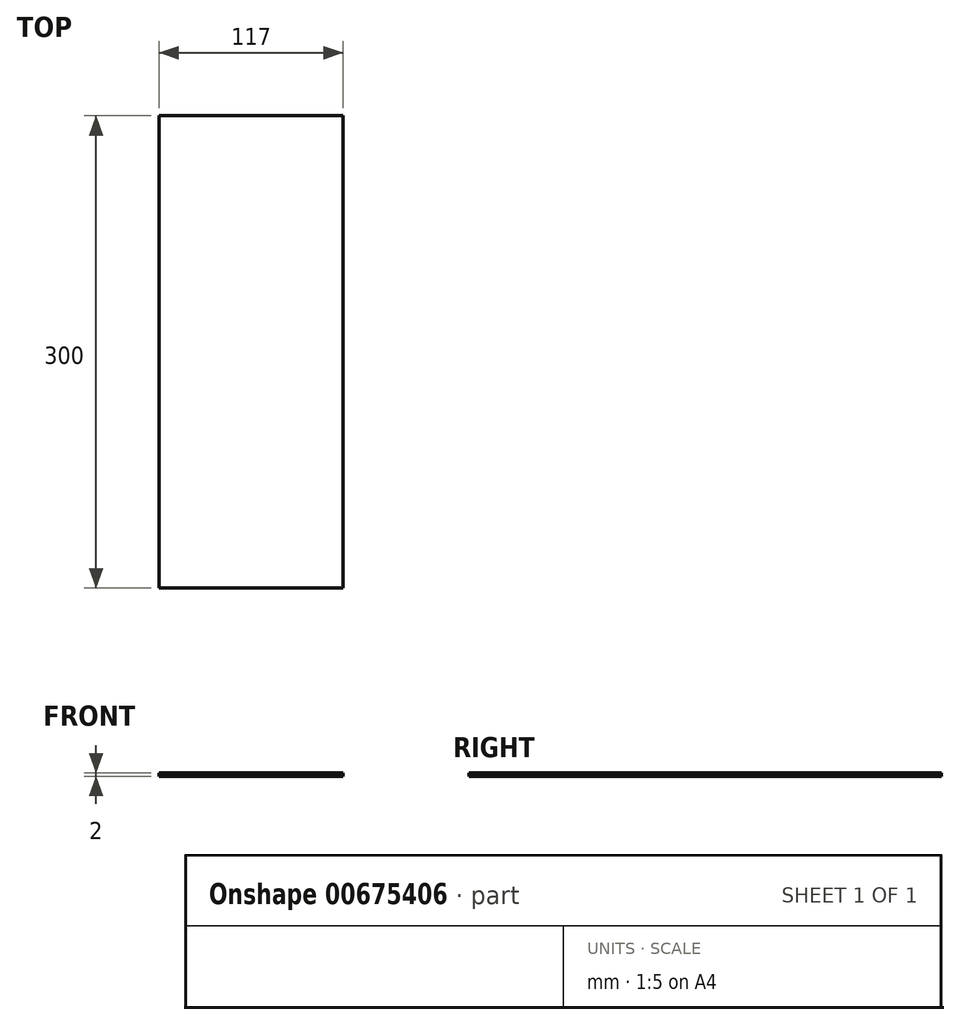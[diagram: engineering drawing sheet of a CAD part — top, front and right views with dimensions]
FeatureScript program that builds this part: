
annotation { "Feature Type Name" : "Feature", "Feature Type Description" : "" }
export const myFeature = defineFeature(function(context is Context, id is Id, definition is map)
    precondition{}
    {
        {
            var Q0;
            Q0=qCreatedBy(makeId("Top.planeOp"),FACE);
            var sketch = newSketch(context, id + "F0", { "sketchPlane" : qUnion([Q0])});
            skLineSegment(sketch, "E0.bottom", {"start": v(0, 0) * mm, "end": v(117, 0) * mm});
            skLineSegment(sketch, "E0.top", {"start": v(0, 300) * mm, "end": v(117, 300) * mm});
            skLineSegment(sketch, "E0.left", {"start": v(0, 0) * mm, "end": v(0, 300) * mm});
            skLineSegment(sketch, "E0.right", {"start": v(117, 0) * mm, "end": v(117, 300) * mm});
            skSolve(sketch);
        }
        {
            var Q0;
            Q0=makeQuery(id+"F0.imprint","IMPRINT",FACE,{"disambiguationData":[TD([[makeQuery(id+"F0.imprint","IMPRINT",EDGE,{"derivedFrom":sQuery(id+"F0.wireOp",EDGE,"E0.bottom")}),1.0]])]});
            extrude(context, id + "F1", {"entities" : qUnion([Q0]), "depth" : 2 * mm, "offsetDistance" : 25 * mm});
        }
    });
